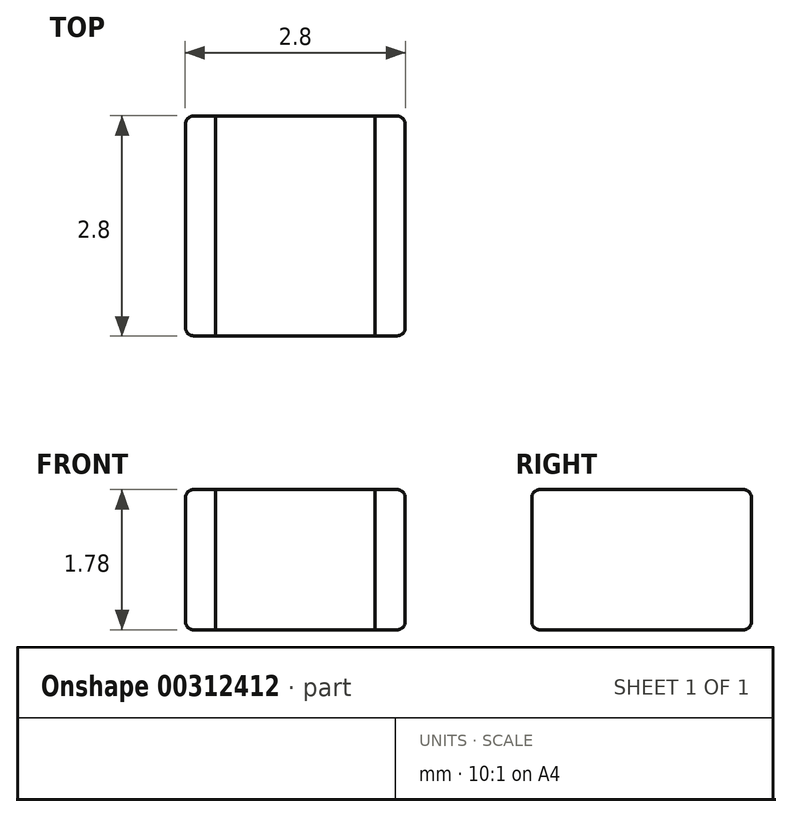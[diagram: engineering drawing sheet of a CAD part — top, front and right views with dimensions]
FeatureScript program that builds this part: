
annotation { "Feature Type Name" : "Feature", "Feature Type Description" : "" }
export const myFeature = defineFeature(function(context is Context, id is Id, definition is map)
    precondition{}
    {
        {
            assignVariable(context, id + "F0", {"name" : "T", "anyValue" : 1.78});
        }
        {
            assignVariable(context, id + "F1", {"name" : "r", "anyValue" : 0.1});
        }
        {
            var Q0;
            Q0=qCreatedBy(makeId("Top.planeOp"),FACE);
            var sketch = newSketch(context, id + "F2", { "sketchPlane" : qUnion([Q0])});
            skLineSegment(sketch, "E0.bottom", {"start": v(1.01, 1.4) * mm, "end": v(-1.02, 1.4) * mm});
            skLineSegment(sketch, "E0.top", {"start": v(1.02, -1.4) * mm, "end": v(-1.01, -1.4) * mm});
            skLineSegment(sketch, "E0.left", {"start": v(1.01, 1.4) * mm, "end": v(1.02, -1.4) * mm});
            skLineSegment(sketch, "E0.right", {"start": v(-1.02, 1.4) * mm, "end": v(-1.01, -1.4) * mm});
            skPoint(sketch, "E0.middle", {"position": v(0, 0) * mm});
            skLineSegment(sketch, "E1", {"start": v(1.01, 1.4) * mm, "end": v(1.4, 1.4) * mm});
            skLineSegment(sketch, "E2", {"start": v(1.4, 1.4) * mm, "end": v(1.4, -1.4) * mm});
            skLineSegment(sketch, "E3", {"start": v(1.4, -1.4) * mm, "end": v(1.02, -1.4) * mm});
            skLineSegment(sketch, "E4", {"start": v(-1.01, -1.4) * mm, "end": v(-1.4, -1.4) * mm});
            skLineSegment(sketch, "E5", {"start": v(-1.4, -1.4) * mm, "end": v(-1.4, 1.4) * mm});
            skLineSegment(sketch, "E6", {"start": v(-1.4, 1.4) * mm, "end": v(-1.02, 1.4) * mm});
            skSolve(sketch);
        }
        {
            var Q0;
            Q0=makeQuery(id+"F2.imprint","IMPRINT",FACE,{"disambiguationData":[TD([[makeQuery(id+"F2.imprint","IMPRINT",EDGE,{"derivedFrom":sQuery(id+"F2.wireOp",EDGE,"E0.bottom")}),1.0]])]});
            extrude(context, id + "F3", {"entities" : qUnion([Q0]), "endBound" : BoundingType.SYMMETRIC, "depth" : (getVariable(context, 'T')) * mm});
        }
        {
            var Q0;
            Q0=makeQuery(id+"F2.imprint","IMPRINT",FACE,{"disambiguationData":[TD([[makeQuery(id+"F2.imprint","IMPRINT",EDGE,{"derivedFrom":sQuery(id+"F2.wireOp",EDGE,"E0.right")}),-1.0]])]});
            extrude(context, id + "F4", {"entities" : qUnion([Q0]), "endBound" : BoundingType.SYMMETRIC, "depth" : (getVariable(context, 'T')) * mm});
        }
        {
            var Q0;
            Q0=makeQuery(id+"F2.imprint","IMPRINT",FACE,{"disambiguationData":[TD([[makeQuery(id+"F2.imprint","IMPRINT",EDGE,{"derivedFrom":sQuery(id+"F2.wireOp",EDGE,"E0.left")}),1.0]])]});
            extrude(context, id + "F5", {"entities" : qUnion([Q0]), "endBound" : BoundingType.SYMMETRIC, "depth" : (getVariable(context, 'T')) * mm});
        }
        {
            var Q0;
            Q0=makeQuery(id+"F4.opExtrude","CAP_EDGE",EDGE,{"disambiguationData":[OSD([sQuery(id+"F2.wireOp",EDGE,"E4")])],"isStart":false});
            var Q1;
            Q1=makeQuery(id+"F3.opExtrude","CAP_EDGE",EDGE,{"disambiguationData":[OSD([sQuery(id+"F2.wireOp",EDGE,"E0.top")])],"isStart":false});
            var Q2;
            Q2=makeQuery(id+"F5.opExtrude","CAP_EDGE",EDGE,{"disambiguationData":[OSD([sQuery(id+"F2.wireOp",EDGE,"E3")])],"isStart":false});
            var Q3;
            Q3=makeQuery(id+"F5.opExtrude","SWEPT_FACE",FACE,{"disambiguationData":[OSD([sQuery(id+"F2.wireOp",EDGE,"E2")])]});
            var Q4;
            Q4=makeQuery(id+"F5.opExtrude","CAP_EDGE",EDGE,{"disambiguationData":[OSD([sQuery(id+"F2.wireOp",EDGE,"E3")])],"isStart":true});
            var Q5;
            Q5=makeQuery(id+"F3.opExtrude","CAP_EDGE",EDGE,{"disambiguationData":[OSD([sQuery(id+"F2.wireOp",EDGE,"E0.top")])],"isStart":true});
            var Q6;
            Q6=makeQuery(id+"F4.opExtrude","CAP_EDGE",EDGE,{"disambiguationData":[OSD([sQuery(id+"F2.wireOp",EDGE,"E4")])],"isStart":true});
            var Q7;
            Q7=makeQuery(id+"F3.opExtrude","CAP_EDGE",EDGE,{"disambiguationData":[OSD([sQuery(id+"F2.wireOp",EDGE,"E0.bottom")])],"isStart":false});
            var Q8;
            Q8=makeQuery(id+"F5.opExtrude","CAP_EDGE",EDGE,{"disambiguationData":[OSD([sQuery(id+"F2.wireOp",EDGE,"E1")])],"isStart":false});
            var Q9;
            Q9=makeQuery(id+"F5.opExtrude","CAP_EDGE",EDGE,{"disambiguationData":[OSD([sQuery(id+"F2.wireOp",EDGE,"E1")])],"isStart":true});
            var Q10;
            Q10=makeQuery(id+"F4.opExtrude","SWEPT_FACE",FACE,{"disambiguationData":[OSD([sQuery(id+"F2.wireOp",EDGE,"E5")])]});
            var Q11;
            Q11=makeQuery(id+"F4.opExtrude","CAP_EDGE",EDGE,{"disambiguationData":[OSD([sQuery(id+"F2.wireOp",EDGE,"E6")])],"isStart":true});
            var Q12;
            Q12=makeQuery(id+"F3.opExtrude","CAP_EDGE",EDGE,{"disambiguationData":[OSD([sQuery(id+"F2.wireOp",EDGE,"E0.bottom")])],"isStart":true});
            var Q13;
            Q13=makeQuery(id+"F4.opExtrude","CAP_EDGE",EDGE,{"disambiguationData":[OSD([sQuery(id+"F2.wireOp",EDGE,"E6")])],"isStart":false});
            fillet(context, id + "F6", {"entities" : qUnion([Q0, Q1, Q2, Q3, Q4, Q5, Q6, Q7, Q8, Q9, Q10, Q11, Q12, Q13]), "radius" : (getVariable(context, 'r')) * mm, "tangentPropagation" : true, "allowEdgeOverflow" : false});
        }
    });
